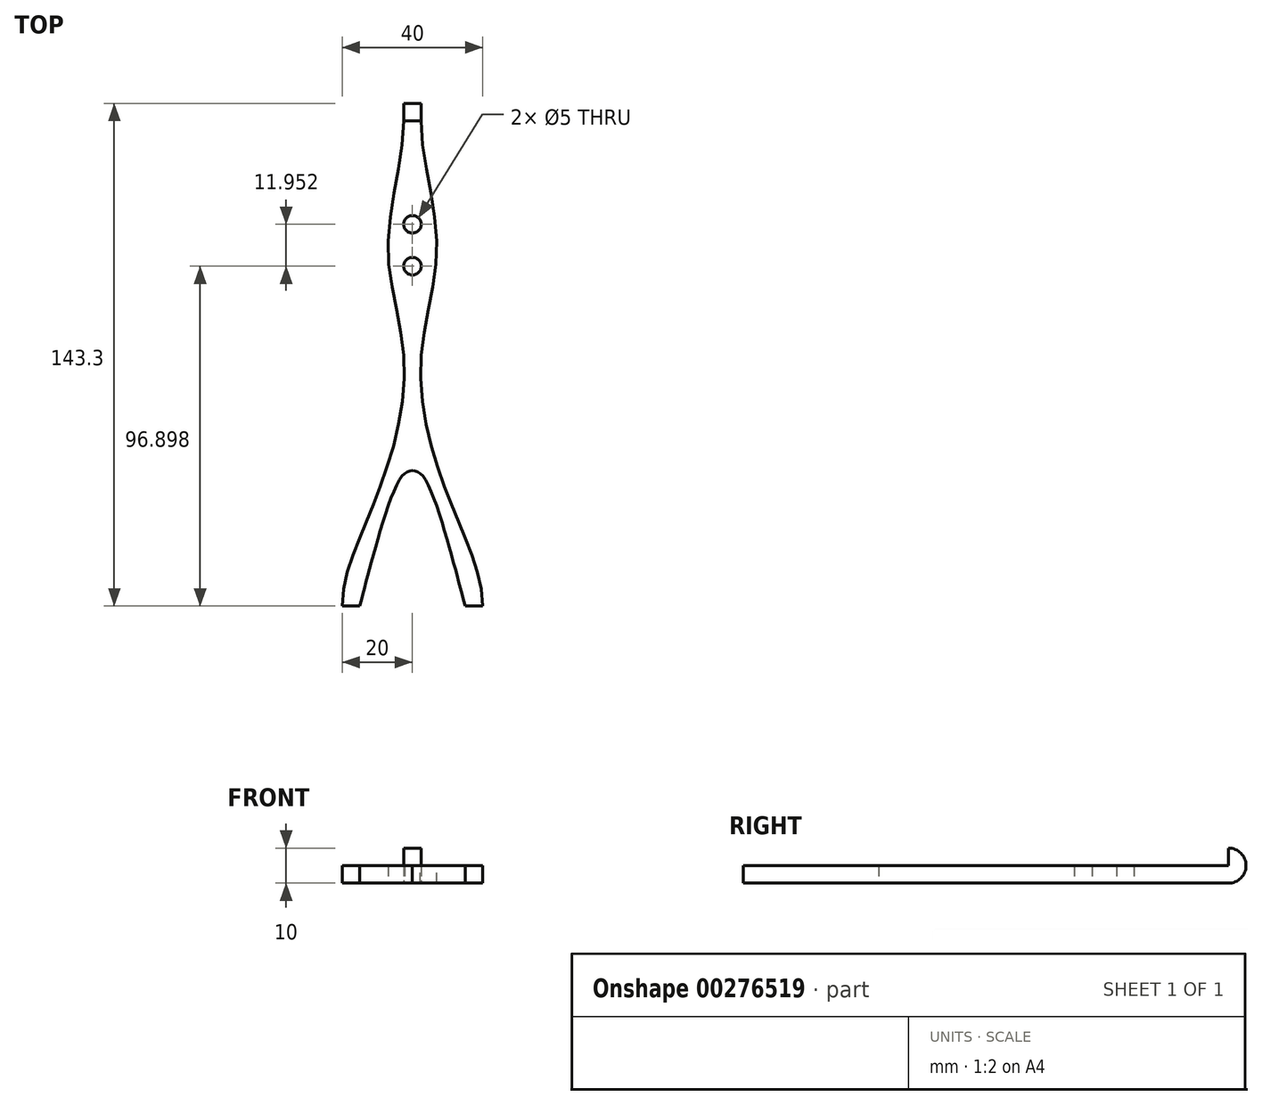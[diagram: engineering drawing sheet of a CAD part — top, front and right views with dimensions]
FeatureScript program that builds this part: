
annotation { "Feature Type Name" : "Feature", "Feature Type Description" : "" }
export const myFeature = defineFeature(function(context is Context, id is Id, definition is map)
    precondition{}
    {
        {
            var Q0;
            Q0=qCreatedBy(makeId("Top.planeOp"),FACE);
            var sketch = newSketch(context, id + "F0", { "sketchPlane" : qUnion([Q0])});
            skFitSpline(sketch, "E0", {"points": [v(-2.5, 71.05) * mm, v(-6.98, 35.3) * mm, v(-2.35, 2.84) * mm, v(-7.46, -28.3) * mm, v(-15.51, -48.99) * mm, v(-20, -67.25) * mm], "startDerivative": vector(0, -155.56) * mm, "endDerivative": vector(2.14, -113.18) * mm});
            skFitSpline(sketch, "E1.MirrorCS", {"points": [v(2.5, 71.05) * mm, v(6.98, 35.3) * mm, v(2.35, 2.84) * mm, v(7.46, -28.3) * mm, v(15.51, -48.99) * mm, v(20, -67.25) * mm], "startDerivative": vector(0, -155.56) * mm, "endDerivative": vector(-2.14, -113.18) * mm});
            skLineSegment(sketch, "E2", {"start": v(2.5, 71.05) * mm, "end": v(-2.5, 71.05) * mm});
            skLineSegment(sketch, "E3", {"start": v(20, -67.25) * mm, "end": v(15, -67.25) * mm});
            skLineSegment(sketch, "E4.MirrorCS", {"start": v(-20, -67.25) * mm, "end": v(-15, -67.25) * mm});
            skFitSpline(sketch, "E5", {"points": [v(15, -67.25) * mm, v(10.47, -50.36) * mm, v(2.85, -30.06) * mm, v(0, -28.63) * mm], "startDerivative": vector(-9.95, 38.44) * mm, "endDerivative": vector(-16.68, 2.55) * mm});
            skFitSpline(sketch, "E6.MirrorCS", {"points": [v(-15, -67.25) * mm, v(-10.47, -50.36) * mm, v(-2.85, -30.06) * mm, v(0, -28.63) * mm], "startDerivative": vector(9.95, 38.44) * mm, "endDerivative": vector(16.68, 2.55) * mm});
            skCircle(sketch, "E7", {"center": v(0, 29.65) * mm, "radius": 2.5 * mm});
            skCircle(sketch, "E8.0.1.0", {"center": v(0, 41.6) * mm, "radius": 2.5 * mm});
            skLineSegment(sketch, "E8.direction1", {"start": v(0, 29.65) * mm, "end": v(16.3, 29.65) * mm, "construction": true});
            skLineSegment(sketch, "E8.direction2", {"start": v(0, 29.65) * mm, "end": v(0, 41.6) * mm, "construction": true});
            skSolve(sketch);
        }
        {
            var Q0;
            Q0=makeQuery(id+"F0.imprint","IMPRINT",FACE,{"disambiguationData":[TD([[makeQuery(id+"F0.imprint","IMPRINT",EDGE,{"derivedFrom":sQuery(id+"F0.wireOp",EDGE,"E0")}),1.0]])]});
            extrude(context, id + "F1", {"entities" : qUnion([Q0]), "depth" : 5 * mm});
        }
        {
            var Q0;
            Q0=makeQuery(id+"F1.opExtrude","SWEPT_FACE",FACE,{"disambiguationData":[OSD([sQuery(id+"F0.wireOp",EDGE,"E2")])]});
            var Q1;
            Q1=makeQuery(id+"F1.opExtrude","CAP_EDGE",EDGE,{"disambiguationData":[OSD([sQuery(id+"F0.wireOp",EDGE,"E2")])],"isStart":false});
            revolve(context, id + "F2", {"operationType" : NewBodyOperationType.ADD, "entities" : qUnion([Q0]), "axis" : qUnion([Q1]), "revolveType" : RevolveType.ONE_DIRECTION, "oppositeDirection" : true, "angle" : 180 * degree});
        }
    });
